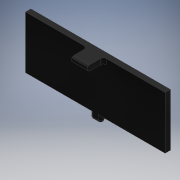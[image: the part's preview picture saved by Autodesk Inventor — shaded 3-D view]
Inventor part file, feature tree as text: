
AUTODESK INVENTOR PART (.ipt)
format: ipt  version: 2018 (Build 220112000, 112)  size: 134,144 bytes
history: native  units: in
note: dims shown in document units (in); Inventor stores cm internally (conversion verified against a paired STEP export)
features: reference x4, other x3, extrude x2, fillet x2, sketch x2
ambient origin geometry x8: Origin, YZ Plane, XZ Plane, XY Plane, X Axis, Y Axis, Z Axis, Center Point
bodies: Solid1 (feature_tree)
feature tree (13):
  extrude  "Extrusion1"  Depth=0.05in TaperAngle=0.0deg
  fillet  "Fillet1"  Radius=0.025in
  extrude  "Extrusion2"  Depth=0.025in
  fillet  "Fillet2"  Radius=0.075in
  sketch  "Sketch1"  dims[d0=0.025in d1=0.05in d2=0.0in d3=0.025in]
  reference  "Reference1"
  reference  "Reference4"
  reference  "Reference5"
  reference  "Reference6"
  sketch  "Sketch2"  dims[d4=0.05in d5=0.075in d6=0.075in d7=0.15in d8=0.0in d9=0.025in]
  other  "<userpath>\Documents\Commodore Cube Project\Case\Assembly.iam"
  other  "Assembly.iam"
  other  "Tray:1"
